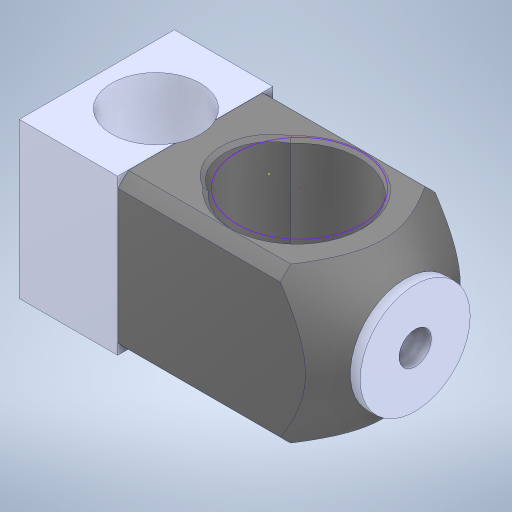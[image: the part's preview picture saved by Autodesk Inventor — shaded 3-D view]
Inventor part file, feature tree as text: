
AUTODESK INVENTOR PART (.ipt)
format: ipt  version: 2023 (Build 270158000, 158)  size: 337,920 bytes
history: mixed  units: in
note: dims shown in document units (in); Inventor stores cm internally (conversion verified against a paired STEP export)
features: sketch x8, extrude x7, other x1, imported_body x1
ambient origin geometry x8: Origin, YZ Plane, XZ Plane, XY Plane, X Axis, Y Axis, Z Axis, Center Point
bodies: Solid1 (imported_parasolid)
feature tree (17):
  other  "6669-001-1-solid1"
  extrude  "Extrusion1"  Depth=0.3937in
  sketch  "Sketch2"  dims[d8=0.3937in d9=0.0in d10=0.0in d11=0.0in]
  extrude  "Extrusion4"  TaperAngle=0.0deg  [1 undecoded]
  sketch  "Sketch5"  dims[d16=0.2362in d17=0.1969in]
  extrude  "Extrusion5"  Depth=0.3937in TaperAngle=0.0deg
  extrude  "Extrusion6"  Depth=0.1969in
  extrude  "Extrusion7"  Depth=0.3543in
  extrude  "Extrusion8"  Depth=0.0197in
  extrude  "Extrusion9"  Depth=0.0197in
  sketch  "Sketch1"  dims[d0=0.3937in d1=0.0in d7=0.1299in]
  sketch  "Sketch4"  dims[d12=0.0394in d13=0.0in d14=0.3937in d15=0.0in]
  sketch  "Sketch6"  dims[d18=0.1969in d19=0.0in d20=0.3543in]
  sketch  "Sketch7"  dims[d21=0.0in d22=0.0in d2=0.0197in]
  sketch  "Sketch8"  dims[d3=0.0344in d4=0.0197in]
  sketch  "Sketch9"  dims[d5=0.0344in]
  imported_body  NMx_Import_Brep_tag  [imported B-rep: ~14 faces, bbox_mm=[22.836, 10.765997, 12.379599]]
note: 1 required parameter value undecoded (feature->parameter linkage not recoverable at this tier; creation-order binding heuristic only, values carry confidence <= 0.55)
